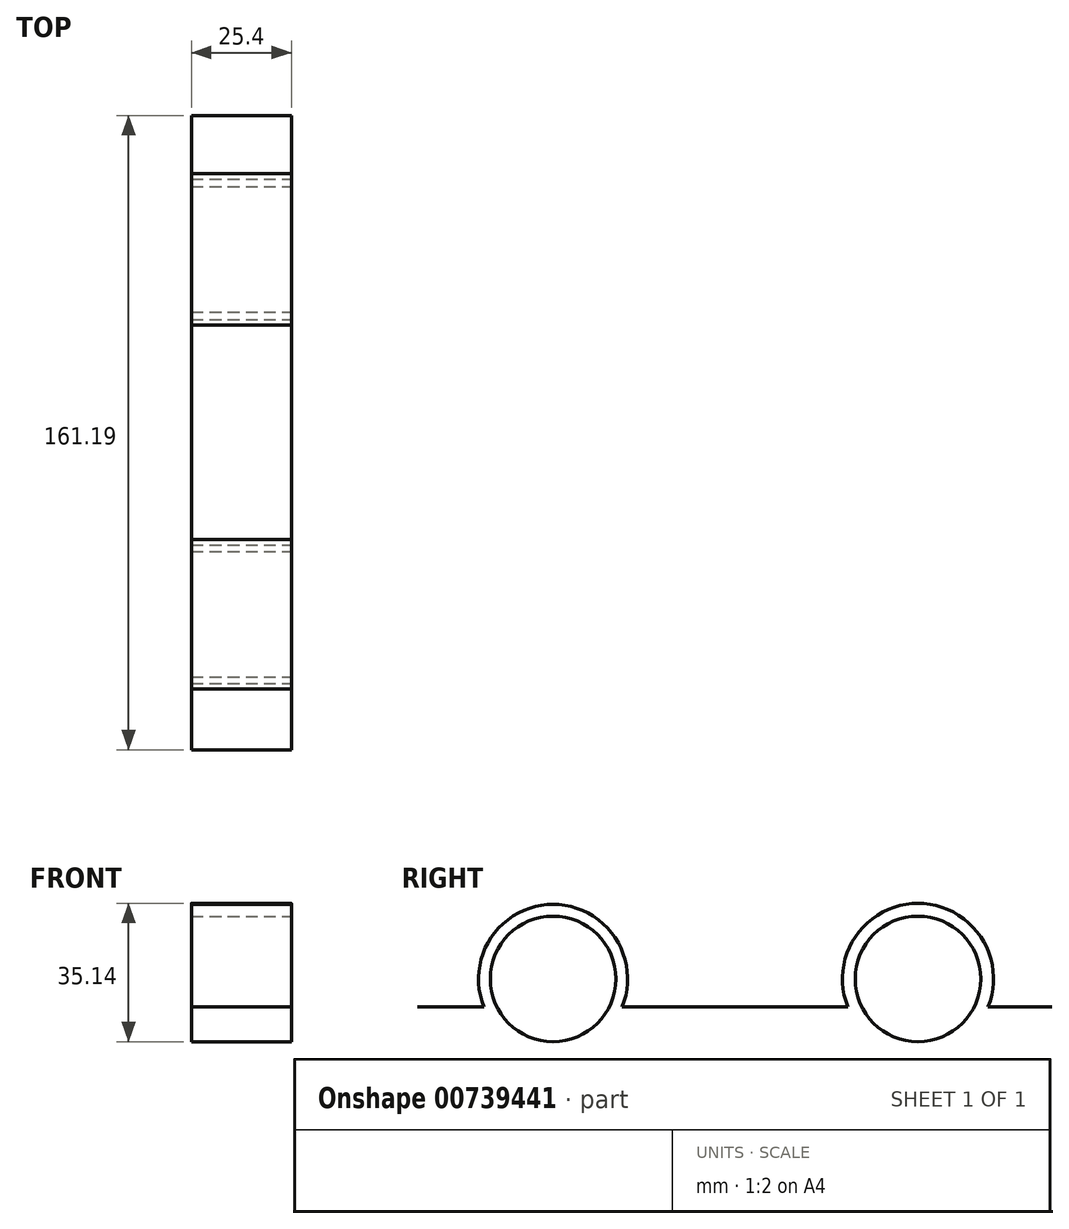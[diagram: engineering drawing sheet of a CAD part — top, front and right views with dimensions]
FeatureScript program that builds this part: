
annotation { "Feature Type Name" : "Feature", "Feature Type Description" : "" }
export const myFeature = defineFeature(function(context is Context, id is Id, definition is map)
    precondition{}
    {
        {
            var Q0;
            Q0=qCreatedBy(makeId("Right.planeOp"),FACE);
            var sketch = newSketch(context, id + "F0", { "sketchPlane" : qUnion([Q0])});
            skCircle(sketch, "E0", {"center": v(-52.42, 0) * mm, "radius": 15.94 * mm});
            skCircle(sketch, "E1.1.0.0", {"center": v(40.3, 0) * mm, "radius": 15.94 * mm});
            skLineSegment(sketch, "E1.direction1", {"start": v(-52.42, 0) * mm, "end": v(40.3, 0) * mm, "construction": true});
            skArc(sketch, "E2", {"start": v(-34.88, -7.15) * mm, "mid": v(-52.42, 18.94) * mm, "end": v(-69.95, -7.15) * mm});
            skArc(sketch, "E3", {"start": v(58.1, -7.15) * mm, "mid": v(40.3, 19.2) * mm, "end": v(22.48, -7.15) * mm});
            skLineSegment(sketch, "E4", {"start": v(-86.87, -7.15) * mm, "end": v(-69.95, -7.15) * mm});
            skLineSegment(sketch, "E5.trimOffspring", {"start": v(-34.88, -7.15) * mm, "end": v(22.48, -7.15) * mm});
            skLineSegment(sketch, "E6.trimOffspring", {"start": v(58.1, -7.15) * mm, "end": v(74.32, -7.15) * mm});
            skSolve(sketch);
        }
        {
            var Q0;
            Q0=sQuery(id+"F0.wireOp",EDGE,"E0");
            var Q1;
            Q1=sQuery(id+"F0.wireOp",EDGE,"E5.trimOffspring");
            var Q2;
            Q2=sQuery(id+"F0.wireOp",EDGE,"E1.1.0.0");
            var Q3;
            Q3=sQuery(id+"F0.wireOp",EDGE,"E6.trimOffspring");
            var Q4;
            Q4=sQuery(id+"F0.wireOp",EDGE,"E3");
            var Q5;
            Q5=sQuery(id+"F0.wireOp",EDGE,"E4");
            var Q6;
            Q6=sQuery(id+"F0.wireOp",EDGE,"E2");
            extrude(context, id + "F1", {"bodyType" : ToolBodyType.SURFACE, "surfaceEntities" : qUnion([Q0, Q1, Q2, Q3, Q4, Q5, Q6]), "depth" : 25.4 * mm, "offsetDistance" : 25.4 * mm});
        }
    });
